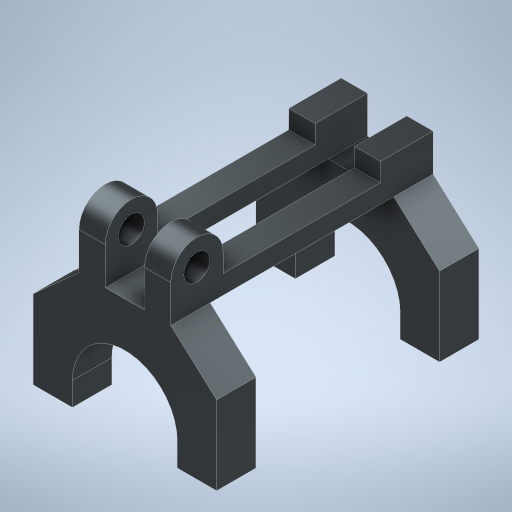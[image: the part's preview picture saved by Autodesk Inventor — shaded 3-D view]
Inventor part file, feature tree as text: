
AUTODESK INVENTOR PART (.ipt)
format: ipt  version: 2024 (Build 280153000, 153)  size: 331,776 bytes
history: native  units: in
note: dims shown in document units (in); Inventor stores cm internally (conversion verified against a paired STEP export)
features: extrude x2, other x2, fillet x1
ambient origin geometry x8: Origin, YZ Plane, XZ Plane, XY Plane, X Axis, Y Axis, Z Axis, Center Point
bodies: Solid1 (feature_tree)
feature tree (5):
  extrude  "front profile Extrusion"  Depth=3.5in
  extrude  "side profile extrusion"  Depth=4.0in
  fillet  "Front Fillet"  Radius=0.875in
  other  "front profile"
  other  "side profile"
